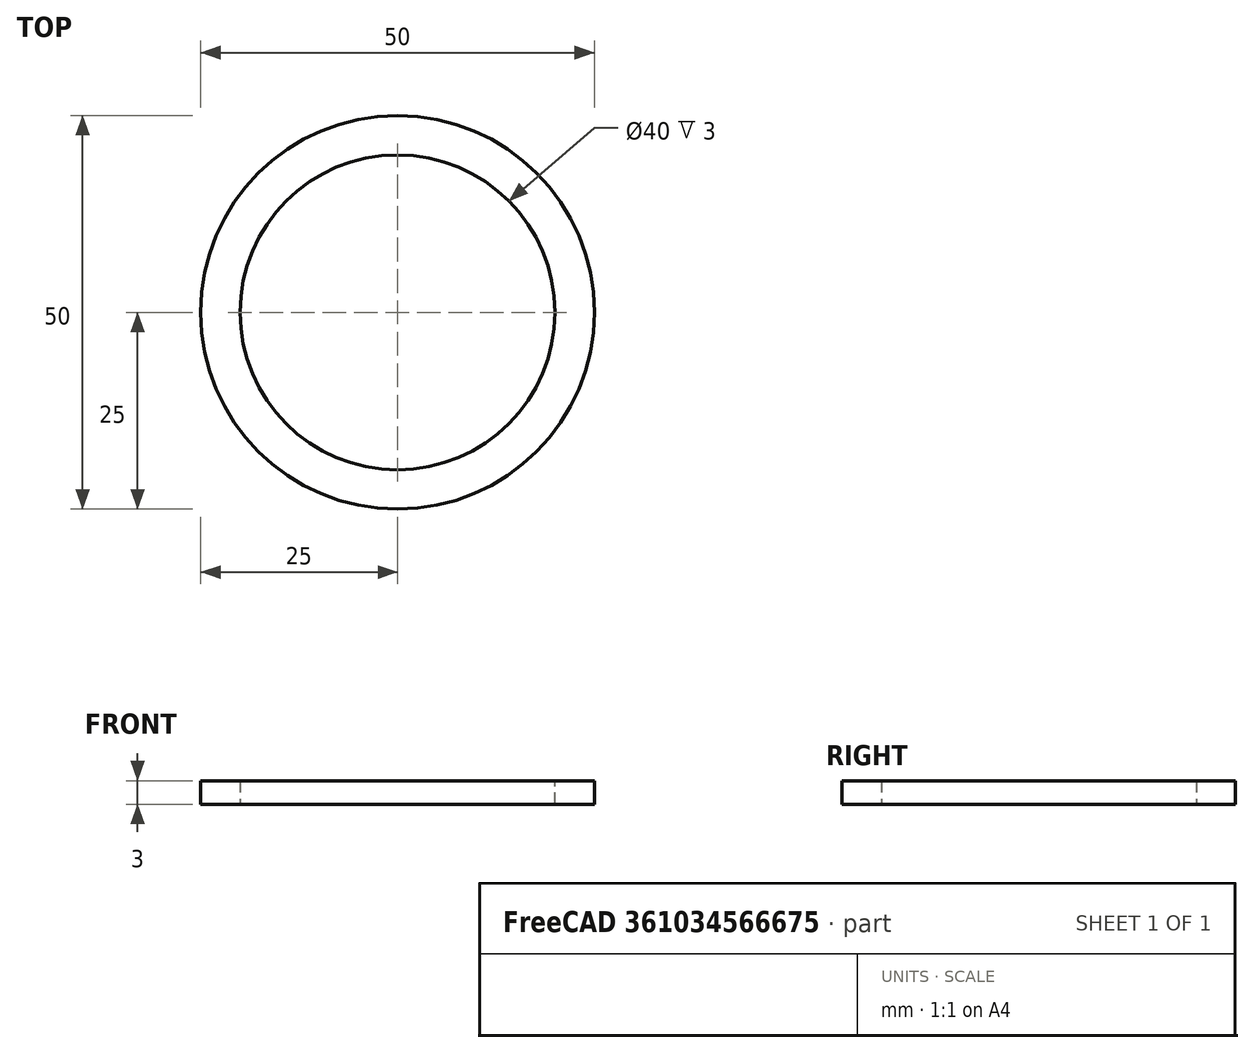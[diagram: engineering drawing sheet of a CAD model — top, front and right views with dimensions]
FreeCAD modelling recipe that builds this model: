
FCSTD DOCUMENT  (FreeCAD 0.17R13543 (Git))
Label: C1022-3
License: All rights reserved
LicenseURL: http://en.wikipedia.org/wiki/All_rights_reserved
objects: Sketcher::SketchObject×1, PartDesign::Pad×1, TechDraw::DrawSVGTemplate×1, TechDraw::DrawProjGroupItem×1, TechDraw::DrawProjGroup×1, TechDraw::DrawPage×1
note: 3 computed .brp shape members not serialized (recipe doc carries the construction recipe); baked Part::Feature solids carry a one-line shape summary decoded from their .brp

FEATURE [Sketcher::SketchObject] Sketch
  MapMode = 5
  sketch-geometry (3):
    g0: Circle CenterX=0 CenterY=0 CenterZ=0 NormalX=0 NormalY=0 NormalZ=1 AngleXU=0 Radius=25
    g1: Circle CenterX=0 CenterY=0 CenterZ=0 NormalX=0 NormalY=0 NormalZ=1 AngleXU=0 Radius=20
    g2: LineSegment [constr] StartX=-20 StartY=0 StartZ=0 EndX=-25 EndY=0 EndZ=0
  constraints (9):
    c: PointOnObject(g0,g-1)
    c: Coincident(g0,g-1)
    c: Coincident(g1,g-1)
    c: Radius(g1) = 20
    c: PointOnObject(g2,g1)
    c: PointOnObject(g2,g0)
    c: Horizontal(g2)
    c: PointOnObject(g2,g-1)
    c: DistanceX(g2,g2) = 5
FEATURE [PartDesign::Pad] Pad  label="Main Axis Spacer"
  Length = 3
  Length2 = 100
  Profile = -> Sketch
  Type = 0
FEATURE [TechDraw::DrawSVGTemplate] Template
  Height = 210
  Orientation = 1
  Width = 297
FEATURE [TechDraw::DrawProjGroupItem] ProjItem  label="Front"
  CoarseView = false
  Direction = (0,0,-1)
  Focus = 100
  HardHidden = false
  IsoCount = 0
  IsoHidden = false
  IsoVisible = false
  LockPosition = false
  Perspective = false
  Rotation = 0
  RotationVector = (1,0,0)
  ScaleType = 0
  SeamHidden = false
  SeamVisible = false
  SmoothHidden = false
  SmoothVisible = false
  Source = -> [Pad]
  Type = 0
  X = 0
  Y = 0
FEATURE [TechDraw::DrawProjGroup] ProjGroup
  Anchor = -> ProjItem
  AutoDistribute = true
  CubeDirs = (6) [(0,1,-6.12323e-17),(0,-6.12323e-17,-1),(-1,0,0),(0,6.12323e-17,1),(1,0,0),(0,-1,6.12323e-17)]
  CubeRotations = (6) [(1,0,0),(1,0,0),(0,6.12323e-17,-1),(-1,0,0),(0,-6.12323e-17,1),(1,0,0)]
  LockPosition = false
  ProjectionType = 0
  Rotation = 0
  ScaleType = 2
  Source = -> [Pad]
  Views = -> [ProjItem]
  X = 148.5
  Y = 105
  spacingX = 15
  spacingY = 15
FEATURE [TechDraw::DrawPage] Page
  KeepUpdated = true
  ProjectionType = 0
  Template = -> Template
  Views = -> [ProjGroup]
